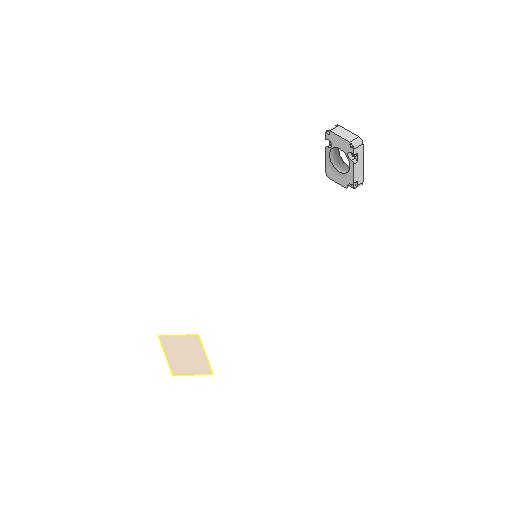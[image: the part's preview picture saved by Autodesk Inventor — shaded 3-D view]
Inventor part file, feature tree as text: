
AUTODESK INVENTOR PART (.ipt)
format: ipt  version: 2022 (Build 260153000, 153)  size: 173,056 bytes
history: native  units: mm
features: other x5, reference x3, plane x2, sketch x2, extrude x1, hole x1, fillet x1
ambient origin geometry x8: Origin, YZ Plane, XZ Plane, XY Plane, X Axis, Y Axis, Z Axis, Center Point
bodies: Volumenkörper1 (feature_tree)
feature tree (15):
  plane  "Arbeitsebene1"
  sketch  "Skizze1"  dims[d0=1.8mm d1=1.8mm]
  plane  "Arbeitsebene2"
  extrude  "Extrusion1"  Depth=1.8mm
  hole  "Bohrung1"  [1 undecoded]
  fillet  "Rundung2"  Radius=10.0mm
  reference  "Referenz1"
  reference  "Referenz2"
  sketch  "Skizze2"  dims[d3=1.8mm d4=20.0mm d5=10.0mm d6=0.0mm d8=3.2mm d9=6.0mm d10=6.5mm d11=3.5mm d12=90.0deg d13=8.0mm d14=20.594885mm d15=2.0mm]
  reference  "Referenz3"
  other  "Assembly_Autofocus_ke400_adjustable.iam"
  other  "Assembly_Cube_SEEED_Xiao_Sense_Camera_adapter_v3:1"
  other  "00_ESP32_XIAO_Adapter_base:1"
  other  "00_KES400:1"
  other  "00_KES400_Bluray_Lens:1"
note: 1 required parameter value undecoded (feature->parameter linkage not recoverable at this tier; creation-order binding heuristic only, values carry confidence <= 0.55)
